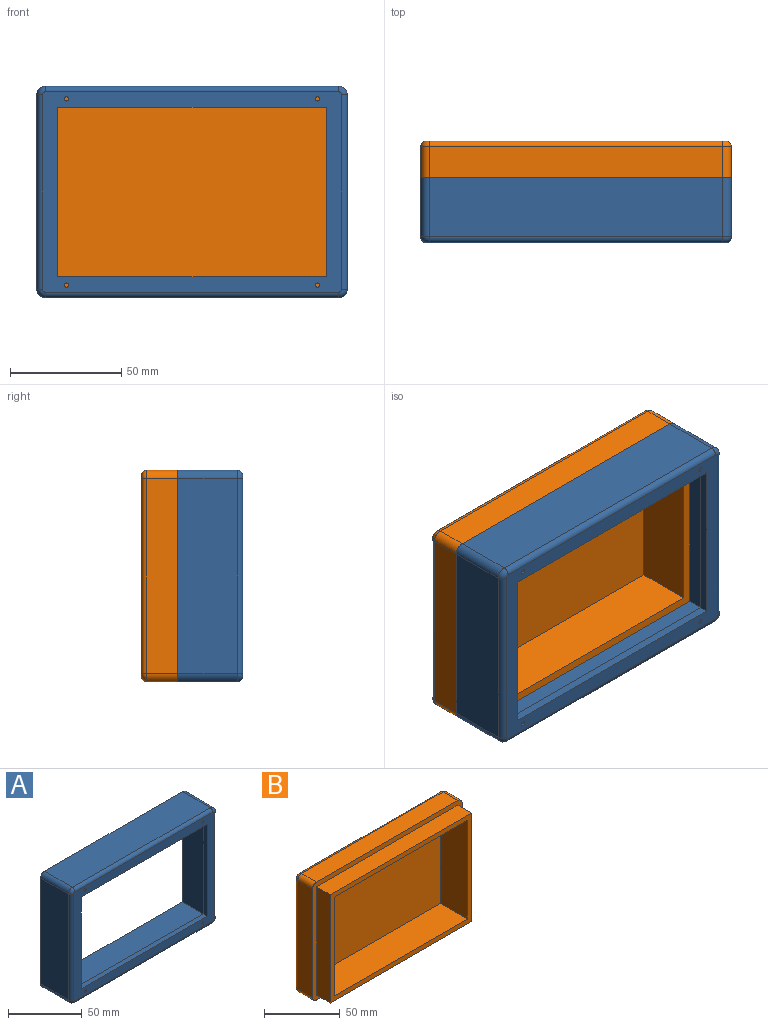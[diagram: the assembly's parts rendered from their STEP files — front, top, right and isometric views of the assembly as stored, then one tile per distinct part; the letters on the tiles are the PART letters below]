
ASSEMBLY  parts=2 mates=1
PART A: 31 faces, bbox 139.7x29.2x95.3 mm
  f0: plane 132.08x87.63mm, normal (0,1,0), area 2369.2mm2, adj f1,f2,f3,f8,f9,f10,f11,f12
  f1: plane 76.2x3.81mm, normal (-1,0,0), area 290.3mm2, adj f0,f2,f12,f13
  f2: plane 120.65x3.81mm, normal (0,0,1), area 459.7mm2, adj f0,f1,f3,f13
  f3: plane 76.2x3.81mm, normal (1,0,0), area 290.3mm2, adj f0,f2,f12,f13
  f4: plane 132.08x26.67mm, normal (0,0,-1), area 3522.6mm2, adj f18,f19,f22,f29
  f5: plane 87.63x26.67mm, normal (1,0,0), area 2337.1mm2, adj f18,f19,f20,f25
  f6: plane 132.08x26.67mm, normal (0,0,1), area 3522.6mm2, adj f18,f20,f21,f24
  f7: plane 87.63x26.67mm, normal (-1,0,0), area 2337.1mm2, adj f18,f21,f22,f28
  f8: cylinder r=0.95mm len=3.81mm, axis (0,1,0), area 22.8mm2, adj f0,f13
  f9: cylinder r=0.95mm len=3.81mm, axis (0,1,0), area 22.8mm2, adj f0,f13
  f10: cylinder r=0.95mm len=3.81mm, axis (0,1,0), area 22.8mm2, adj f0,f13
  f11: cylinder r=0.95mm len=3.81mm, axis (0,1,0), area 22.8mm2, adj f0,f13
  f12: plane 120.65x3.81mm, normal (0,0,-1), area 459.7mm2, adj f0,f1,f3,f13
  f13: plane 134.62x90.17mm, normal (0,-1,0), area 2932.4mm2, adj f1,f2,f3,f8,f9,f10,f11,f12
  f14: plane 87.63x25.4mm, normal (1,0,0), area 2225.8mm2, adj f0,f15,f17,f18
  f15: plane 132.08x25.4mm, normal (0,0,1), area 3354.8mm2, adj f0,f14,f16,f18
  f16: plane 87.63x25.4mm, normal (-1,0,0), area 2225.8mm2, adj f0,f15,f17,f18
  f17: plane 132.08x25.4mm, normal (0,0,-1), area 3354.8mm2, adj f0,f14,f16,f18
  f18: plane 139.7x95.25mm, normal (0,1,0), area 1719.8mm2, adj f4,f5,f6,f7,f14,f15,f16,f17
  f19: cylinder r=3.81mm len=26.67mm, axis (0,1,0), area 159.6mm2, adj f4,f5,f18,f27
  f20: cylinder r=3.81mm len=26.67mm, axis (0,-1,0), area 159.6mm2, adj f5,f6,f18,f23
  f21: cylinder r=3.81mm len=26.67mm, axis (0,1,0), area 159.6mm2, adj f6,f7,f18,f26
  f22: cylinder r=3.81mm len=26.67mm, axis (0,-1,0), area 159.6mm2, adj f4,f7,f18,f30
  f23: torus R=1.27mm, axis (0,-1,0), area 18.1mm2, adj f13,f20,f24,f25
  f24: cylinder r=2.54mm len=132.08mm, axis (1,0,0), area 527mm2, adj f6,f13,f23,f26
  f25: cylinder r=2.54mm len=87.63mm, axis (0,0,-1), area 349.6mm2, adj f5,f13,f23,f27
  f26: torus R=1.27mm, axis (0,-1,0), area 18.1mm2, adj f13,f21,f24,f28
  f27: torus R=1.27mm, axis (0,-1,0), area 18.1mm2, adj f13,f19,f25,f29
  f28: cylinder r=2.54mm len=87.63mm, axis (0,0,1), area 349.6mm2, adj f7,f13,f26,f30
  f29: cylinder r=2.54mm len=132.08mm, axis (-1,0,0), area 527mm2, adj f4,f13,f27,f30
  f30: torus R=1.27mm, axis (0,-1,0), area 18.1mm2, adj f13,f22,f28,f29
PART B: 28 faces, bbox 139.7x29.2x95.3 mm
  f0: plane 87.63x13.97mm, normal (-1,0,0), area 1224.2mm2, adj f5,f6,f9,f13
  f1: plane 132.08x13.97mm, normal (0,0,-1), area 1845.2mm2, adj f5,f6,f7,f17
  f2: plane 87.63x13.97mm, normal (1,0,0), area 1224.2mm2, adj f5,f7,f8,f14
  f3: plane 132.08x13.97mm, normal (0,0,1), area 1845.2mm2, adj f5,f8,f9,f10
  f4: plane 134.62x90.17mm, normal (0,1,0), area 12137.3mm2, adj f10,f11,f12,f13,f14,f15,f16,f17
  f5: plane 139.7x95.25mm, normal (0,-1,0), area 1719.8mm2, adj f0,f1,f2,f3,f6,f7,f8,f9
  f6: cylinder r=3.81mm len=13.97mm, axis (0,-1,0), area 83.6mm2, adj f0,f1,f5,f15
  f7: cylinder r=3.81mm len=13.97mm, axis (0,1,0), area 83.6mm2, adj f1,f2,f5,f16
  f8: cylinder r=3.81mm len=13.97mm, axis (0,-1,0), area 83.6mm2, adj f2,f3,f5,f12
  f9: cylinder r=3.81mm len=13.97mm, axis (0,1,0), area 83.6mm2, adj f0,f3,f5,f11
  f10: cylinder r=2.54mm len=132.08mm, axis (1,0,0), area 527mm2, adj f3,f4,f11,f12
  f11: torus R=1.27mm, axis (0,-1,0), area 18.1mm2, adj f4,f9,f10,f13
  f12: torus R=1.27mm, axis (0,-1,0), area 18.1mm2, adj f4,f8,f10,f14
  f13: cylinder r=2.54mm len=87.63mm, axis (0,0,1), area 349.6mm2, adj f0,f4,f11,f15
  f14: cylinder r=2.54mm len=87.63mm, axis (0,0,-1), area 349.6mm2, adj f2,f4,f12,f16
  f15: torus R=1.27mm, axis (0,-1,0), area 18.1mm2, adj f4,f6,f13,f17
  f16: torus R=1.27mm, axis (0,-1,0), area 18.1mm2, adj f4,f7,f14,f17
  f17: cylinder r=2.54mm len=132.08mm, axis (-1,0,0), area 527mm2, adj f1,f4,f15,f16
  f18: plane 132.08x12.7mm, normal (0,0,-1), area 1677.4mm2, adj f5,f19,f21,f26
  f19: plane 87.63x12.7mm, normal (-1,0,0), area 1112.9mm2, adj f5,f18,f20,f26
  f20: plane 132.08x12.7mm, normal (0,0,1), area 1677.4mm2, adj f5,f19,f21,f26
  f21: plane 87.63x12.7mm, normal (1,0,0), area 1112.9mm2, adj f5,f18,f20,f26
  f22: plane 80.01x25.4mm, normal (-1,0,0), area 2032.3mm2, adj f23,f25,f26,f27
  f23: plane 124.46x25.4mm, normal (0,0,1), area 3161.3mm2, adj f22,f24,f26,f27
  f24: plane 80.01x25.4mm, normal (1,0,0), area 2032.3mm2, adj f23,f25,f26,f27
  f25: plane 124.46x25.4mm, normal (0,0,-1), area 3161.3mm2, adj f22,f24,f26,f27
  f26: plane 132.08x87.63mm, normal (0,-1,0), area 1616.1mm2, adj f18,f19,f20,f21,f22,f23,f24,f25
  f27: plane 124.46x80.01mm, normal (0,-1,0), area 9958mm2, adj f22,f23,f24,f25
PLACE A at identity
PLACE B t=(0,-63.5,0)mm
MATE parallel B.f5 <-> A.f18  axis (0,-1,0) through (0,25.4,0)mm
